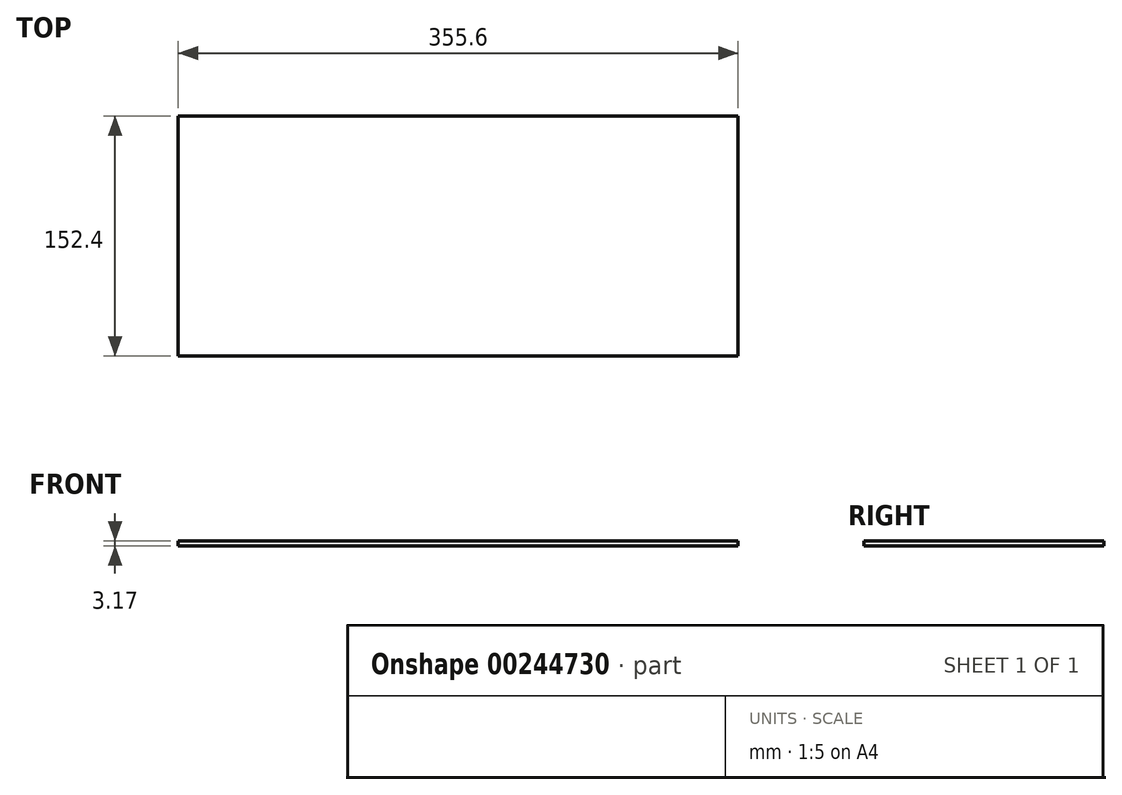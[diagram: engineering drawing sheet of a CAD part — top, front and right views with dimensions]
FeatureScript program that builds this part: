
annotation { "Feature Type Name" : "Feature", "Feature Type Description" : "" }
export const myFeature = defineFeature(function(context is Context, id is Id, definition is map)
    precondition{}
    {
        {
            var Q0;
            Q0=qCreatedBy(makeId("Top.planeOp"),FACE);
            var sketch = newSketch(context, id + "F0", { "sketchPlane" : qUnion([Q0])});
            skLineSegment(sketch, "E0.bottom", {"start": v(-177.8, 76.2) * mm, "end": v(177.8, 76.2) * mm});
            skLineSegment(sketch, "E0.top", {"start": v(-177.8, -76.2) * mm, "end": v(177.8, -76.2) * mm});
            skLineSegment(sketch, "E0.left", {"start": v(-177.8, 76.2) * mm, "end": v(-177.8, -76.2) * mm});
            skLineSegment(sketch, "E0.right", {"start": v(177.8, 76.2) * mm, "end": v(177.8, -76.2) * mm});
            skPoint(sketch, "E0.middle", {"position": v(0, 0) * mm});
            skSolve(sketch);
        }
        {
            var Q0;
            Q0=makeQuery(id+"F0.imprint","IMPRINT",FACE,{"disambiguationData":[TD([[makeQuery(id+"F0.imprint","IMPRINT",EDGE,{"derivedFrom":sQuery(id+"F0.wireOp",EDGE,"E0.bottom")}),-1.0]])]});
            extrude(context, id + "F1", {"entities" : qUnion([Q0]), "depth" : 3.17 * mm});
        }
    });
